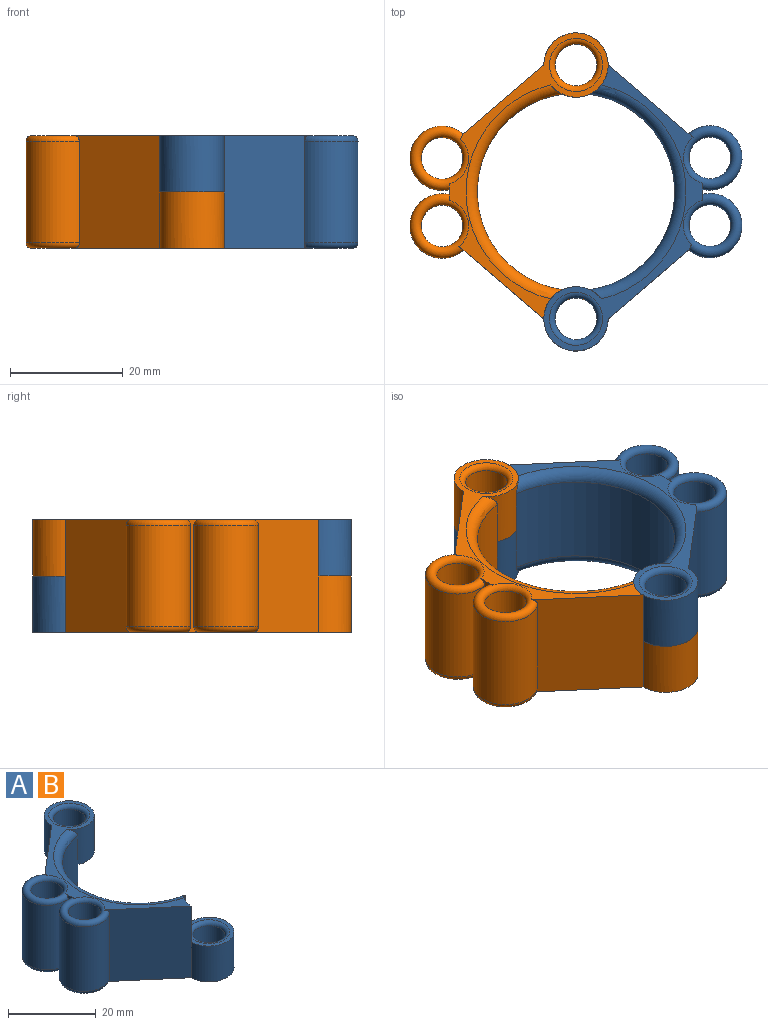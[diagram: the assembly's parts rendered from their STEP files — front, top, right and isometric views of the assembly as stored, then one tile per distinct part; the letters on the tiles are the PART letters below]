
ASSEMBLY  parts=2 mates=1
PART A: 29 faces, bbox 35.9x56.8x20.1 mm
  f0: cylinder r=5.7mm len=10mm, axis (0,0,-1), area 63.4mm2, adj f1,f6,f8,f11,f19
  f1: plane 20x14.3mm, normal (-0.65,0.76,0), area 375.8mm2, adj f0,f2,f7,f8,f10
  f2: cylinder r=22.5mm len=20mm, axis (0,0,-1), area 1.1mm2, adj f1,f7,f8,f17,f21,f22
  f3: cylinder r=22.5mm len=20mm, axis (0,0,-1), area 18.4mm2, adj f7,f8,f15,f17,f21,f22,f23,f24
  f4: plane 20.08x15.14mm, normal (-0.65,-0.76,0), area 375.9mm2, adj f5,f7,f8,f12,f15,f23,f24
  f5: cylinder r=5.7mm len=10mm, axis (0,0,-1), area 63.4mm2, adj f4,f6,f7,f14,f20
  f6: cylinder r=17.5mm len=34.67mm, axis (0,0,-1), area 802.3mm2, adj f0,f5,f10,f12,f19,f20
  f7: plane 50.7x28.2mm, normal (0,0,1), area 130.7mm2, adj f1,f2,f3,f4,f5,f10,f20,f21
  f8: plane 50.7x28.2mm, normal (0,0,-1), area 130.7mm2, adj f0,f1,f2,f3,f4,f12,f19,f22
  f9: cylinder r=3.7mm len=8mm, axis (0,0,-1), area 186mm2, adj f27,f28
  f10: cylinder r=5.7mm len=11.4mm, axis (0,0,-1), area 294.8mm2, adj f1,f6,f7,f11,f20
  f11: plane 11.4x11.4mm, normal (0,0,-1), area 32.7mm2, adj f0,f10,f27
  f12: cylinder r=5.7mm len=11.4mm, axis (0,0,1), area 294.8mm2, adj f4,f6,f8,f14,f19
  f13: cylinder r=3.7mm len=8mm, axis (0,0,1), area 186mm2, adj f25,f26
  f14: plane 11.4x11.4mm, normal (0,0,1), area 32.7mm2, adj f5,f12,f25
  f15: cylinder r=5.7mm len=18mm, axis (0,0,1), area 418.8mm2, adj f3,f4,f23,f24
  f16: cylinder r=3.7mm len=18mm, axis (0,0,1), area 418.5mm2, adj f23,f24
  f17: cylinder r=5.7mm len=18mm, axis (0,0,1), area 418.1mm2, adj f2,f3,f21,f22
  f18: cylinder r=3.7mm len=18mm, axis (0,0,1), area 418.5mm2, adj f21,f22
  f19: torus R=19.5mm, axis (0,0,1), area 159.1mm2, adj f0,f6,f8,f12
  f20: torus R=19.5mm, axis (0,0,1), area 159.1mm2, adj f5,f6,f7,f10
  f21: torus R=4.7mm, axis (0,0,1), area 74.6mm2, adj f2,f3,f7,f17,f18
  f22: torus R=4.7mm, axis (0,0,1), area 74.6mm2, adj f2,f3,f8,f17,f18
  f23: torus R=4.7mm, axis (0,0,1), area 74.3mm2, adj f3,f4,f7,f15,f16
  f24: torus R=4.7mm, axis (0,0,1), area 74.3mm2, adj f3,f4,f8,f15,f16
  f25: torus R=4.7mm, axis (0,0,1), area 40.1mm2, adj f13,f14
  f26: torus R=4.7mm, axis (0,0,1), area 40.1mm2, adj f8,f13
  f27: torus R=4.7mm, axis (0,0,1), area 40.1mm2, adj f9,f11
  f28: torus R=4.7mm, axis (0,0,1), area 40.1mm2, adj f7,f9
PART B: same geometry as A
PLACE A rot(axis=(0,0,-1),180deg) t=(-34.81,7.61,-3.05)mm
PLACE B rot(axis=(-0.25,0.96,0.13),0deg) t=(-34.81,7.61,-3.05)mm
MATE revolute B.f5 <-> A.f0  axis (0,0,1) through (-34.81,-14.89,-3.05)mm
